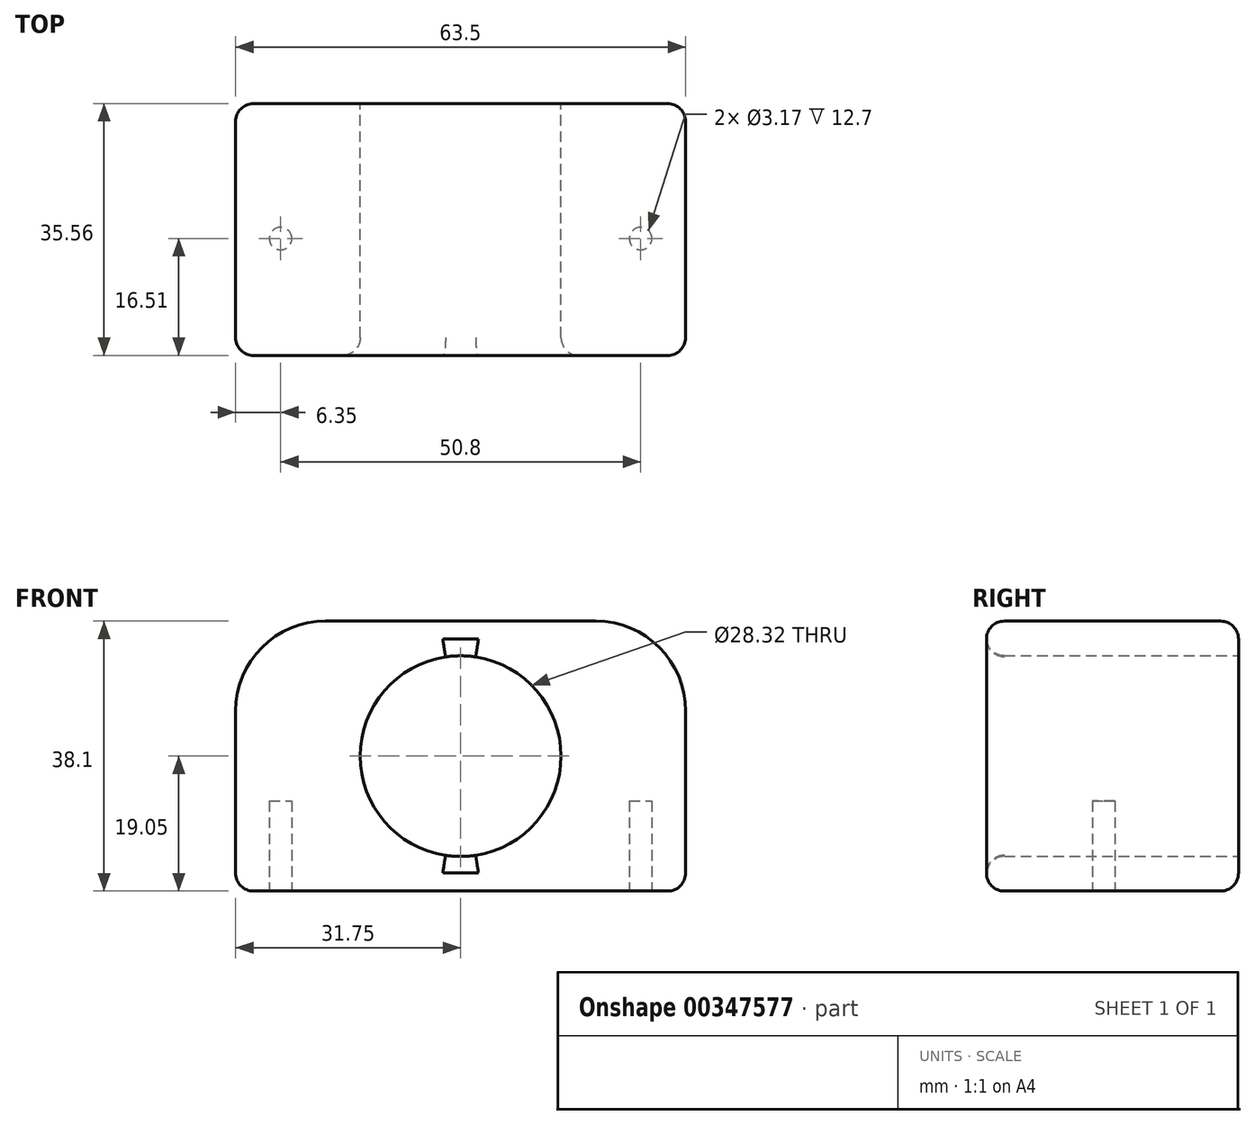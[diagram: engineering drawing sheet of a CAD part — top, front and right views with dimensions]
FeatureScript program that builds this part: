
annotation { "Feature Type Name" : "Feature", "Feature Type Description" : "" }
export const myFeature = defineFeature(function(context is Context, id is Id, definition is map)
    precondition{}
    {
        {
            var Q0;
            Q0=qCreatedBy(makeId("Front.planeOp"),FACE);
            var sketch = newSketch(context, id + "F0", { "sketchPlane" : qUnion([Q0])});
            skLineSegment(sketch, "E0.bottom", {"start": v(0, 0) * mm, "end": v(-63.5, 0) * mm});
            skLineSegment(sketch, "E0.top", {"start": v(0, 38.1) * mm, "end": v(-63.5, 38.1) * mm});
            skLineSegment(sketch, "E0.left", {"start": v(0, 0) * mm, "end": v(0, 38.1) * mm});
            skLineSegment(sketch, "E0.right", {"start": v(-63.5, 0) * mm, "end": v(-63.5, 38.1) * mm});
            skCircle(sketch, "E1", {"center": v(-31.75, 19.05) * mm, "radius": 14.16 * mm});
            skSolve(sketch);
        }
        {
            var Q0;
            Q0 = qSketchRegion(id + "F0", true);
            extrude(context, id + "F1", {"entities" : qUnion([Q0]), "depth" : 35.56 * mm});
        }
        {
            var Q0;
            Q0=makeQuery(id+"F1.opExtrude","SWEPT_FACE",FACE,{"disambiguationData":[OSD([sQuery(id+"F0.wireOp",EDGE,"E0.bottom")])]});
            var sketch = newSketch(context, id + "F2", { "sketchPlane" : qUnion([Q0])});
            skCircle(sketch, "E2", {"center": v(-57.15, 19.05) * mm, "radius": 1.59 * mm});
            skCircle(sketch, "E3", {"center": v(-6.35, 19.05) * mm, "radius": 1.59 * mm});
            skSolve(sketch);
        }
        {
            var Q0;
            Q0 = qSketchRegion(id + "F2", true);
            extrude(context, id + "F3", {"entities" : qUnion([Q0]), "operationType" : NewBodyOperationType.REMOVE, "oppositeDirection" : true, "depth" : 12.7 * mm});
        }
        {
            var Q0;
            Q0=makeQuery(id+"F1.opExtrude","SWEPT_EDGE",EDGE,{"disambiguationData":[OSD([sQuery(id+"F0.wireOp",EDGE,"E0.top"),sQuery(id+"F0.wireOp",EDGE,"E0.right")])]});
            var Q1;
            Q1=makeQuery(id+"F1.opExtrude","SWEPT_EDGE",EDGE,{"disambiguationData":[OSD([sQuery(id+"F0.wireOp",EDGE,"E0.top"),sQuery(id+"F0.wireOp",EDGE,"E0.left")])]});
            fillet(context, id + "F4", {"entities" : qUnion([Q0, Q1]), "radius" : 12.7 * mm, "tangentPropagation" : true, "allowEdgeOverflow" : false});
        }
        {
            var Q0;
            Q0=makeQuery(id+"F1.opExtrude","SWEPT_EDGE",EDGE,{"disambiguationData":[OSD([sQuery(id+"F0.wireOp",EDGE,"E0.bottom"),sQuery(id+"F0.wireOp",EDGE,"E0.right")])]});
            var Q1;
            Q1=makeQuery(id+"F1.opExtrude","SWEPT_EDGE",EDGE,{"disambiguationData":[OSD([sQuery(id+"F0.wireOp",EDGE,"E0.bottom"),sQuery(id+"F0.wireOp",EDGE,"E0.left")])]});
            var Q2;
            Q2=makeQuery(id+"F1.opExtrude","CAP_EDGE",EDGE,{"disambiguationData":[OSD([sQuery(id+"F0.wireOp",EDGE,"E0.bottom")])],"isStart":false});
            var Q3;
            Q3=makeQuery(id+"F1.opExtrude","CAP_EDGE",EDGE,{"disambiguationData":[OSD([sQuery(id+"F0.wireOp",EDGE,"E0.bottom")])],"isStart":true});
            var Q4;
            Q4=makeQuery(id+"F1.opExtrude","CAP_EDGE",EDGE,{"disambiguationData":[OSD([sQuery(id+"F0.wireOp",EDGE,"E0.left")])],"isStart":true});
            var Q5;
            Q5=makeQuery(id+"F1.opExtrude","CAP_EDGE",EDGE,{"disambiguationData":[OSD([sQuery(id+"F0.wireOp",EDGE,"E0.left")])],"isStart":false});
            var Q6;
            Q6=makeQuery(id+"F3.boolean.opBoolean","COPY",EDGE,{"derivedFrom":makeQuery(id+"F3.opExtrude","CAP_EDGE",EDGE,{"disambiguationData":[OSD([sQuery(id+"F2.wireOp",EDGE,"E3")])],"isStart":true})});
            var Q7;
            Q7=makeQuery(id+"F3.boolean.opBoolean","COPY",EDGE,{"derivedFrom":makeQuery(id+"F3.opExtrude","CAP_EDGE",EDGE,{"disambiguationData":[OSD([sQuery(id+"F2.wireOp",EDGE,"E2")])],"isStart":true})});
            fillet(context, id + "F5", {"entities" : qUnion([Q0, Q1, Q2, Q3, Q4, Q5, Q6, Q7]), "radius" : 2.54 * mm, "tangentPropagation" : true, "allowEdgeOverflow" : false});
        }
        {
            var Q0;
            Q0=makeQuery(id+"F1.opExtrude","CAP_EDGE",EDGE,{"disambiguationData":[OSD([sQuery(id+"F0.wireOp",EDGE,"E1")])],"isStart":false});
            fillet(context, id + "F6", {"entities" : qUnion([Q0]), "radius" : 2.54 * mm, "tangentPropagation" : true, "allowEdgeOverflow" : false});
        }
    });
